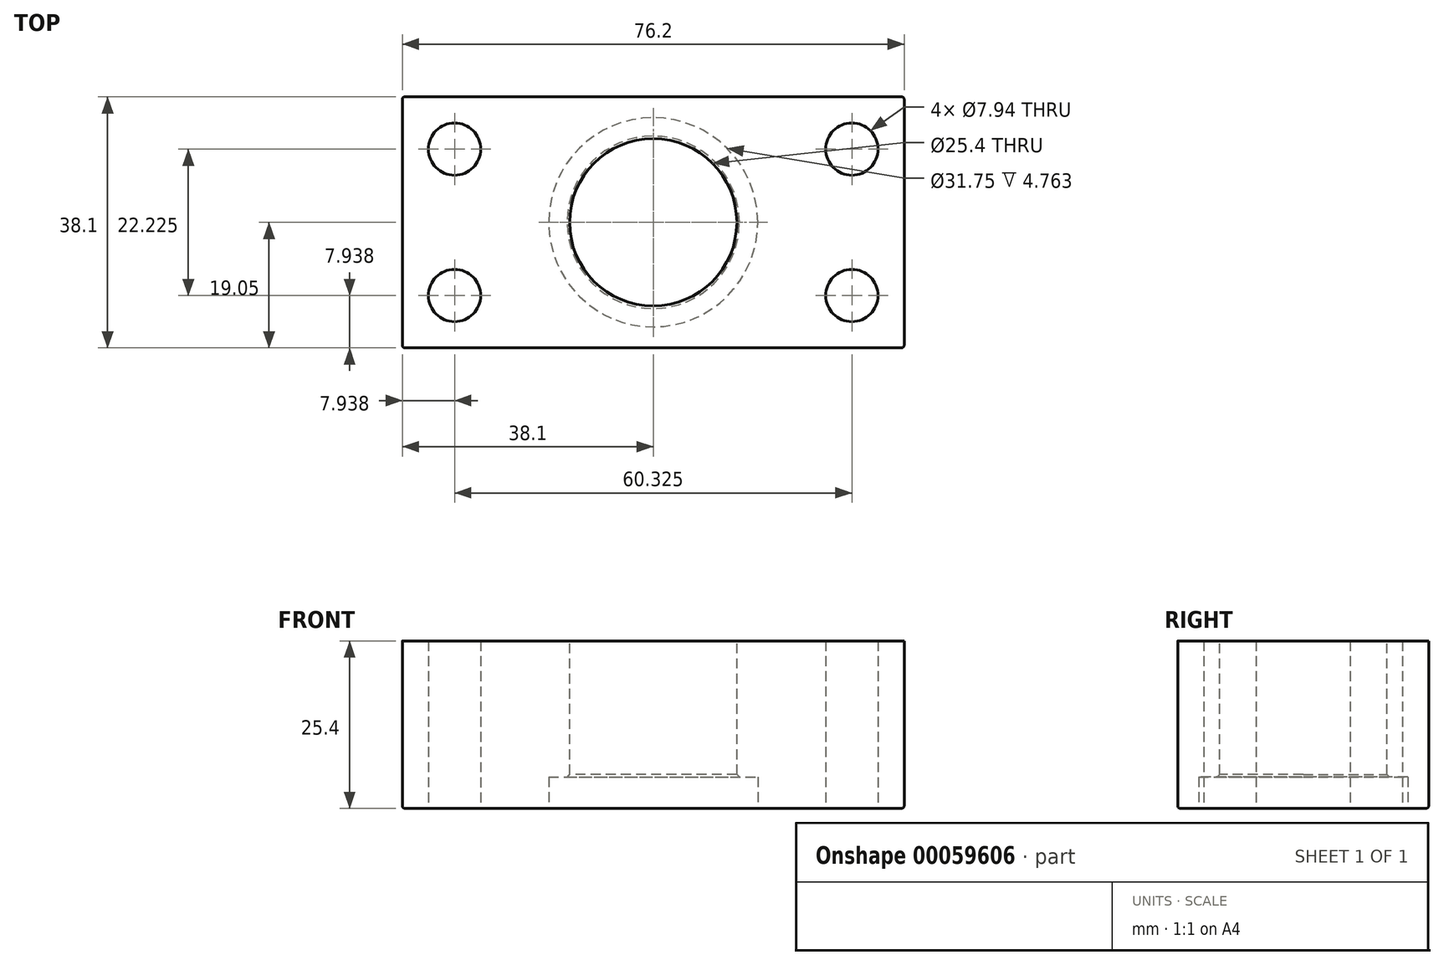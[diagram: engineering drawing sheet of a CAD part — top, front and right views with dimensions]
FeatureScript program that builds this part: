
annotation { "Feature Type Name" : "Feature", "Feature Type Description" : "" }
export const myFeature = defineFeature(function(context is Context, id is Id, definition is map)
    precondition{}
    {
        {
            var Q0;
            Q0=qCreatedBy(makeId("Top.planeOp"),FACE);
            var sketch = newSketch(context, id + "F0", { "sketchPlane" : qUnion([Q0])});
            skLineSegment(sketch, "E0.bottom", {"start": v(38.1, 19.05) * mm, "end": v(-38.1, 19.05) * mm});
            skLineSegment(sketch, "E0.top", {"start": v(38.1, -19.05) * mm, "end": v(-38.1, -19.05) * mm});
            skLineSegment(sketch, "E0.left", {"start": v(38.1, 19.05) * mm, "end": v(38.1, -19.05) * mm});
            skLineSegment(sketch, "E0.right", {"start": v(-38.1, 19.05) * mm, "end": v(-38.1, -19.05) * mm});
            skPoint(sketch, "E0.middle", {"position": v(0, 0) * mm});
            skCircle(sketch, "E1", {"center": v(-30.16, -11.11) * mm, "radius": 3.97 * mm});
            skCircle(sketch, "E2", {"center": v(-30.16, 11.11) * mm, "radius": 3.97 * mm});
            skCircle(sketch, "E3.MirrorC", {"center": v(30.16, -11.11) * mm, "radius": 3.97 * mm});
            skCircle(sketch, "E4.MirrorC", {"center": v(30.16, 11.11) * mm, "radius": 3.97 * mm});
            skSolve(sketch);
        }
        {
            var Q0;
            Q0 = qSketchRegion(id + "F0", true);
            extrude(context, id + "F1", {"entities" : qUnion([Q0]), "depth" : 25.4 * mm});
        }
        {
            var Q0;
            Q0=makeQuery(id+"F1.opExtrude","CAP_EDGE",EDGE,{"disambiguationData":[OSD([sQuery(id+"F0.wireOp",EDGE,"E0.top")])],"isStart":true});
            var Q1;
            Q1=makeQuery(id+"F1.opExtrude","CAP_EDGE",EDGE,{"disambiguationData":[OSD([sQuery(id+"F0.wireOp",EDGE,"E0.left")])],"isStart":true});
            var Q2;
            Q2=makeQuery(id+"F1.opExtrude","CAP_EDGE",EDGE,{"disambiguationData":[OSD([sQuery(id+"F0.wireOp",EDGE,"E0.right")])],"isStart":true});
            fillet(context, id + "F2", {"entities" : qUnion([Q0, Q1, Q2]), "radius" : 0.38 * mm, "tangentPropagation" : true, "allowEdgeOverflow" : false});
        }
        {
            var Q0;
            Q0=makeQuery(id+"F1.opExtrude","CAP_EDGE",EDGE,{"disambiguationData":[OSD([sQuery(id+"F0.wireOp",EDGE,"E0.bottom")])],"isStart":true});
            fillet(context, id + "F3", {"entities" : qUnion([Q0]), "radius" : 0.38 * mm, "tangentPropagation" : true, "allowEdgeOverflow" : false});
        }
        {
            var Q0;
            Q0=makeQuery(id+"F1.opExtrude","SWEPT_EDGE",EDGE,{"disambiguationData":[OSD([sQuery(id+"F0.wireOp",EDGE,"E0.top"),sQuery(id+"F0.wireOp",EDGE,"E0.left")])]});
            var Q1;
            Q1=makeQuery(id+"F1.opExtrude","SWEPT_EDGE",EDGE,{"disambiguationData":[OSD([sQuery(id+"F0.wireOp",EDGE,"E0.top"),sQuery(id+"F0.wireOp",EDGE,"E0.right")])]});
            var Q2;
            {var subQ0=sQuery(id+"F0.wireOp",EDGE,"E0.left");Q2=makeQuery(id+"F3.opFillet","BLEND_EDGE",EDGE,{"blendedFrom":[makeQuery(id+"F1.opExtrude","SWEPT_EDGE",EDGE,{"disambiguationData":[OSD([sQuery(id+"F0.wireOp",EDGE,"E0.bottom"),subQ0])]}),makeQuery(id+"F1.opExtrude","SWEPT_FACE",FACE,{"disambiguationData":[OSD([subQ0])]})],"blendedInto":[makeQuery(id+"F1.opExtrude","SWEPT_FACE",FACE,{"disambiguationData":[OSD([subQ0])]})]});}
            fillet(context, id + "F4", {"entities" : qUnion([Q0, Q1, Q2]), "radius" : 0.38 * mm, "tangentPropagation" : true, "allowEdgeOverflow" : false});
        }
        {
            var Q0;
            Q0=makeQuery(id+"F1.opExtrude","CAP_FACE",FACE,{"disambiguationData":[OSD([sQuery(id+"F0.wireOp",EDGE,"E0.bottom"),sQuery(id+"F0.wireOp",EDGE,"E0.top"),sQuery(id+"F0.wireOp",EDGE,"E0.left"),sQuery(id+"F0.wireOp",EDGE,"E0.right"),sQuery(id+"F0.wireOp",EDGE,"E1"),sQuery(id+"F0.wireOp",EDGE,"E2"),sQuery(id+"F0.wireOp",EDGE,"E3.MirrorC"),sQuery(id+"F0.wireOp",EDGE,"E4.MirrorC")])],"isStart":false});
            var sketch = newSketch(context, id + "F5", { "sketchPlane" : qUnion([Q0])});
            skCircle(sketch, "E5", {"center": v(0, 0) * mm, "radius": 12.7 * mm});
            skSolve(sketch);
        }
        {
            var Q0;
            Q0 = qSketchRegion(id + "F5", true);
            extrude(context, id + "F6", {"entities" : qUnion([Q0]), "operationType" : NewBodyOperationType.REMOVE, "oppositeDirection" : true, "depth" : 25.4 * mm});
        }
        {
            var Q0;
            Q0=makeQuery(id+"F1.opExtrude","CAP_FACE",FACE,{"disambiguationData":[OSD([sQuery(id+"F0.wireOp",EDGE,"E0.bottom"),sQuery(id+"F0.wireOp",EDGE,"E0.top"),sQuery(id+"F0.wireOp",EDGE,"E0.left"),sQuery(id+"F0.wireOp",EDGE,"E0.right"),sQuery(id+"F0.wireOp",EDGE,"E1"),sQuery(id+"F0.wireOp",EDGE,"E2"),sQuery(id+"F0.wireOp",EDGE,"E3.MirrorC"),sQuery(id+"F0.wireOp",EDGE,"E4.MirrorC")])],"isStart":true});
            var sketch = newSketch(context, id + "F7", { "sketchPlane" : qUnion([Q0])});
            skCircle(sketch, "E6", {"center": v(0, 0) * mm, "radius": 15.88 * mm});
            skSolve(sketch);
        }
        {
            var Q0;
            Q0 = qSketchRegion(id + "F7", true);
            extrude(context, id + "F8", {"entities" : qUnion([Q0]), "operationType" : NewBodyOperationType.REMOVE, "oppositeDirection" : true, "depth" : 4.76 * mm});
        }
        {
            var Q0;
            Q0=makeQuery(id+"F8.boolean.opBoolean","INTERSECT",EDGE,{"derivedFrom":[makeQuery(id+"F6.boolean.opBoolean","COPY",FACE,{"derivedFrom":makeQuery(id+"F6.opExtrude","SWEPT_FACE",FACE,{"disambiguationData":[OSD([sQuery(id+"F5.wireOp",EDGE,"E5")])]})}),makeQuery(id+"F8.opExtrude","CAP_FACE",FACE,{"disambiguationData":[OSD([sQuery(id+"F7.wireOp",EDGE,"E6")])],"isStart":false})]});
            chamfer(context, id + "F9", {"entities" : qUnion([Q0]), "width" : 0.38 * mm, "tangentPropagation" : true});
        }
    });
